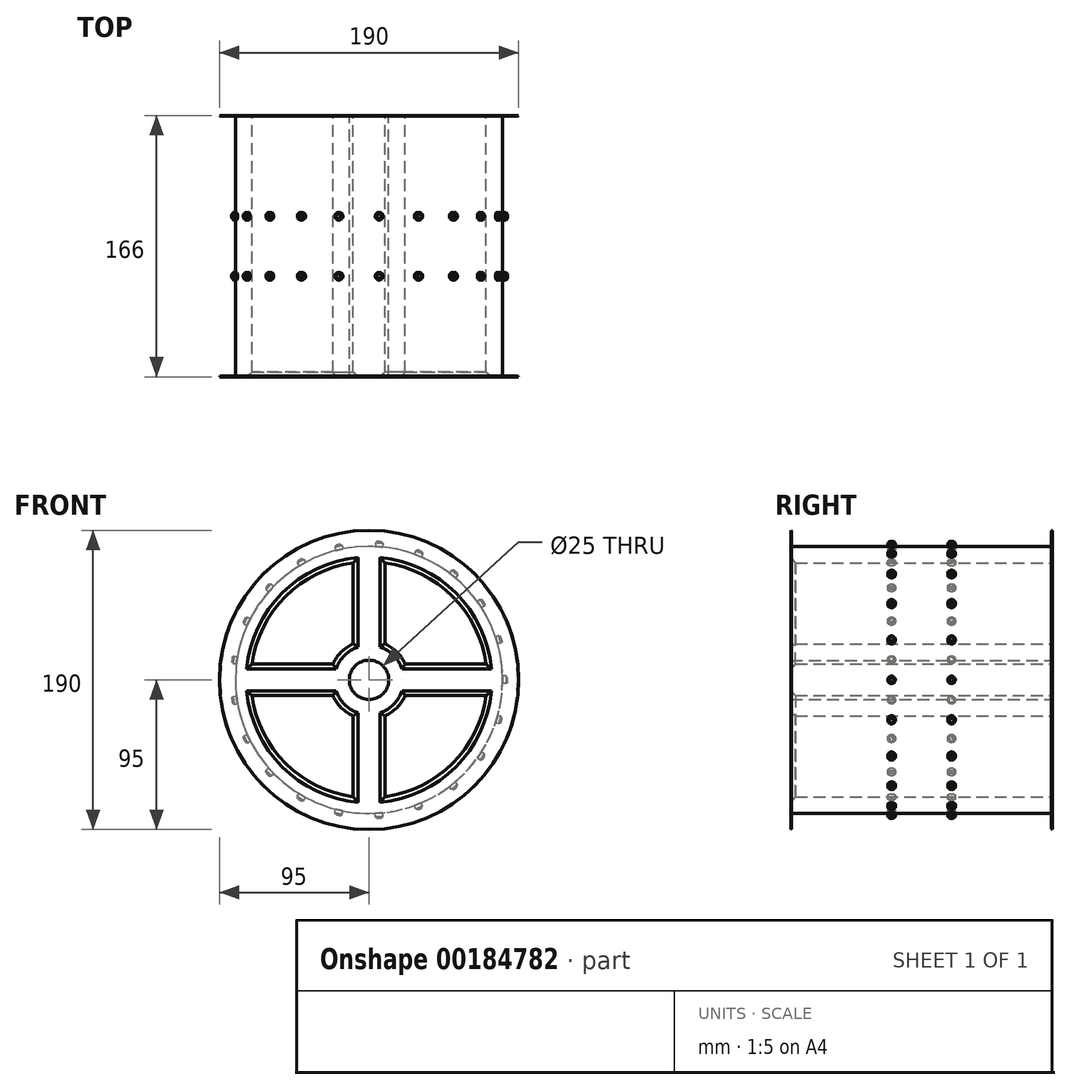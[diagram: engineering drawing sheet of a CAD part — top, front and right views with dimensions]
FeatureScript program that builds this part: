
annotation { "Feature Type Name" : "Feature", "Feature Type Description" : "" }
export const myFeature = defineFeature(function(context is Context, id is Id, definition is map)
    precondition{}
    {
        {
            var Q0;
            Q0=qCreatedBy(makeId("Front.planeOp"),FACE);
            var sketch = newSketch(context, id + "F0", { "sketchPlane" : qUnion([Q0])});
            skCircle(sketch, "E0", {"center": v(0, 0) * mm, "radius": 84.9 * mm});
            skSolve(sketch);
        }
        {
            var Q0;
            Q0=makeQuery(id+"F0.imprint","IMPRINT",FACE,{"disambiguationData":[TD([[makeQuery(id+"F0.imprint","IMPRINT",EDGE,{"derivedFrom":sQuery(id+"F0.wireOp",EDGE,"E0")}),1.0]])]});
            extrude(context, id + "F1", {"entities" : qUnion([Q0]), "depth" : 166 * mm});
        }
        {
            var Q0;
            Q0=makeQuery(id+"F1.opExtrude","CAP_FACE",FACE,{"disambiguationData":[OSD([sQuery(id+"F0.wireOp",EDGE,"E0")])],"isStart":true});
            var sketch = newSketch(context, id + "F2", { "sketchPlane" : qUnion([Q0])});
            skCircle(sketch, "E1", {"center": v(0, 0) * mm, "radius": 95 * mm});
            skSolve(sketch);
        }
        {
            var Q0;
            Q0=makeQuery(id+"F2.imprint","IMPRINT",FACE,{"disambiguationData":[TD([[makeQuery(id+"F2.imprint","IMPRINT",EDGE,{"derivedFrom":sQuery(id+"F2.wireOp",EDGE,"E1")}),1.0]])]});
            var Q1;
            Q1=sQuery(id+"F2.wireOp",EDGE,"E1");
            extrude(context, id + "F3", {"entities" : qUnion([Q0]), "operationType" : NewBodyOperationType.ADD, "surfaceEntities" : qUnion([Q1]), "oppositeDirection" : true, "depth" : .5 * mm});
        }
        {
            var Q0;
            Q0=makeQuery(id+"F1.opExtrude","CAP_FACE",FACE,{"disambiguationData":[OSD([sQuery(id+"F0.wireOp",EDGE,"E0")])],"isStart":false});
            var sketch = newSketch(context, id + "F4", { "sketchPlane" : qUnion([Q0])});
            skCircle(sketch, "E2", {"center": v(0, 0) * mm, "radius": 95 * mm});
            skSolve(sketch);
        }
        {
            var Q0;
            Q0=makeQuery(id+"F4.imprint","IMPRINT",FACE,{"disambiguationData":[TD([[makeQuery(id+"F4.imprint","IMPRINT",EDGE,{"derivedFrom":sQuery(id+"F4.wireOp",EDGE,"E2")}),1.0]])]});
            var Q1;
            Q1=sQuery(id+"F4.wireOp",EDGE,"E2");
            extrude(context, id + "F5", {"entities" : qUnion([Q0]), "operationType" : NewBodyOperationType.ADD, "surfaceEntities" : qUnion([Q1]), "oppositeDirection" : true, "depth" : .5 * mm});
        }
        {
            var Q0;
            Q0=qCreatedBy(makeId("Right.planeOp"),FACE);
            var sketch = newSketch(context, id + "F6", { "sketchPlane" : qUnion([Q0])});
            skCircle(sketch, "E3", {"center": v(-63.95, 0) * mm, "radius": 2.39 * mm});
            skLineSegment(sketch, "E4", {"start": v(-83, -58.64) * mm, "end": v(-83, 58.38) * mm});
            skCircle(sketch, "E5.MirrorC", {"center": v(-102.05, 0) * mm, "radius": 2.39 * mm});
            skSolve(sketch);
        }
        {
            var Q0;
            Q0 = qSketchRegion(id + "F6", true);
            extrude(context, id + "F7", {"entities" : qUnion([Q0]), "depth" : 88 * mm});
        }
        {
            var Q0;
            Q0=makeQuery(id+"F7.opExtrude","CAP_EDGE",EDGE,{"disambiguationData":[OSD([sQuery(id+"F6.wireOp",EDGE,"E3")])],"isStart":false});
            chamfer(context, id + "F8", {"entities" : qUnion([Q0]), "width" : 1 * mm, "tangentPropagation" : true});
        }
        {
            var Q0;
            Q0=makeQuery(id+"F7.opExtrude","SWEPT_BODY",BODY,{"disambiguationData":[OSD([sQuery(id+"F6.wireOp",EDGE,"E3")])]});
            var Q1;
            Q1=makeQuery(id+"F1.opExtrude","SWEPT_FACE",FACE,{"disambiguationData":[OSD([sQuery(id+"F0.wireOp",EDGE,"E0")])]});
            var Q2;
            Q2=makeQuery(id+"F1.opExtrude","SWEPT_BODY",BODY,{"disambiguationData":[OSD([sQuery(id+"F0.wireOp",EDGE,"E0")])]});
            circularPattern(context, id + "F9", {"operationType" : NewBodyOperationType.ADD, "entities" : qUnion([Q0]), "axis" : qUnion([Q1]), "angle" : 17.14 * degree, "instanceCount" : 21});
        }
        {
            var Q0;
            Q0=makeQuery(id+"F7.opExtrude","CAP_EDGE",EDGE,{"disambiguationData":[OSD([sQuery(id+"F6.wireOp",EDGE,"E5.MirrorC")])],"isStart":false});
            chamfer(context, id + "F10", {"entities" : qUnion([Q0]), "width" : 1 * mm, "tangentPropagation" : true});
        }
        {
            var Q0;
            Q0=makeQuery(id+"F7.opExtrude","SWEPT_BODY",BODY,{"disambiguationData":[OSD([sQuery(id+"F6.wireOp",EDGE,"E5.MirrorC")])]});
            var Q1;
            Q1=makeQuery(id+"F1.opExtrude","SWEPT_FACE",FACE,{"disambiguationData":[OSD([sQuery(id+"F0.wireOp",EDGE,"E0")])]});
            circularPattern(context, id + "F11", {"operationType" : NewBodyOperationType.ADD, "entities" : qUnion([Q0]), "axis" : qUnion([Q1]), "angle" : 17.14 * degree, "instanceCount" : 22});
        }
        {
            var Q0;
            Q0=makeQuery(id+"F3.opExtrude","CAP_EDGE",EDGE,{"disambiguationData":[OSD([sQuery(id+"F2.wireOp",EDGE,"E1")])],"isStart":false});
            var Q1;
            Q1=makeQuery(id+"F5.opExtrude","CAP_EDGE",EDGE,{"disambiguationData":[OSD([sQuery(id+"F4.wireOp",EDGE,"E2")])],"isStart":false});
            chamfer(context, id + "F12", {"entities" : qUnion([Q0, Q1]), "width" : .5 * mm, "tangentPropagation" : true});
        }
        {
            var Q0;
            {var subQ0=sQuery(id+"F0.wireOp",EDGE,"E0");Q0=makeQuery(id+"F3.boolean.opBoolean","MERGE",FACE,{"derivedFrom":[makeQuery(id+"F1.opExtrude","CAP_FACE",FACE,{"disambiguationData":[OSD([subQ0])],"isStart":true}),makeQuery(id+"F3.opExtrude","CAP_FACE",FACE,{"disambiguationData":[OSD([subQ0,sQuery(id+"F2.wireOp",EDGE,"E1")])],"isStart":true})]});}
            var sketch = newSketch(context, id + "F13", { "sketchPlane" : qUnion([Q0])});
            skCircle(sketch, "E6", {"center": v(0, 0) * mm, "radius": 75 * mm});
            skCircle(sketch, "E7", {"center": v(0, 0) * mm, "radius": 25 * mm});
            skCircle(sketch, "E8", {"center": v(0, 0) * mm, "radius": 12.5 * mm});
            skLineSegment(sketch, "E9", {"start": v(25, 0) * mm, "end": v(75, 0) * mm});
            skLineSegment(sketch, "E10", {"start": v(-25, 0) * mm, "end": v(-75, 0) * mm});
            skLineSegment(sketch, "E11", {"start": v(0, -25) * mm, "end": v(0, -75) * mm});
            skLineSegment(sketch, "E12", {"start": v(0, 25) * mm, "end": v(0, 75) * mm});
            skLineSegment(sketch, "E13", {"start": v(-22.91, 10) * mm, "end": v(-74.33, 10) * mm});
            skLineSegment(sketch, "E14", {"start": v(-22.91, -10) * mm, "end": v(-74.33, -10) * mm});
            skLineSegment(sketch, "E15", {"start": v(-10, -22.91) * mm, "end": v(-10, -74.33) * mm});
            skLineSegment(sketch, "E16", {"start": v(10, -22.91) * mm, "end": v(10, -74.33) * mm});
            skLineSegment(sketch, "E17", {"start": v(22.91, -10) * mm, "end": v(74.33, -10) * mm});
            skLineSegment(sketch, "E18", {"start": v(22.91, 10) * mm, "end": v(74.33, 10) * mm});
            skLineSegment(sketch, "E19", {"start": v(10, 22.91) * mm, "end": v(10, 74.33) * mm});
            skLineSegment(sketch, "E20", {"start": v(-10, 22.91) * mm, "end": v(-10, 74.33) * mm});
            skSolve(sketch);
        }
        {
            var Q0;
            {var subQ0=sQuery(id+"F13.wireOp",EDGE,"E13");Q0=makeQuery(id+"F13.imprint","IMPRINT",FACE,{"disambiguationData":[TD([[makeQuery(id+"F13.imprint","IMPRINT",EDGE,{"derivedFrom":subQ0}),-1.0]])]});}
            var Q1;
            {var subQ0=sQuery(id+"F13.wireOp",EDGE,"E18");Q1=makeQuery(id+"F13.imprint","IMPRINT",FACE,{"disambiguationData":[TD([[makeQuery(id+"F13.imprint","IMPRINT",EDGE,{"derivedFrom":subQ0}),1.0]])]});}
            var Q2;
            {var subQ0=sQuery(id+"F13.wireOp",EDGE,"E14");Q2=makeQuery(id+"F13.imprint","IMPRINT",FACE,{"disambiguationData":[TD([[makeQuery(id+"F13.imprint","IMPRINT",EDGE,{"derivedFrom":subQ0}),1.0]])]});}
            var Q3;
            {var subQ0=sQuery(id+"F13.wireOp",EDGE,"E16");Q3=makeQuery(id+"F13.imprint","IMPRINT",FACE,{"disambiguationData":[TD([[makeQuery(id+"F13.imprint","IMPRINT",EDGE,{"derivedFrom":subQ0}),1.0]])]});}
            var Q4;
            Q4=makeQuery(id+"F13.imprint","IMPRINT",FACE,{"disambiguationData":[TD([[makeQuery(id+"F13.imprint","IMPRINT",EDGE,{"derivedFrom":sQuery(id+"F13.wireOp",EDGE,"E8")}),1.0]])]});
            extrude(context, id + "F14", {"entities" : qUnion([Q0, Q1, Q2, Q3, Q4]), "operationType" : NewBodyOperationType.REMOVE, "endBound" : BoundingType.THROUGH_ALL, "oppositeDirection" : true, "depth" : 25.4 * mm});
        }
        {
            var Q0;
            {var subQ0=sQuery(id+"F13.wireOp",EDGE,"E6");var subQ1=sQuery(id+"F0.wireOp",EDGE,"E0");Q0=makeQuery(id+"F14.boolean.opBoolean","INTERSECT",EDGE,{"derivedFrom":[makeQuery(id+"F5.boolean.opBoolean","MERGE",FACE,{"derivedFrom":[makeQuery(id+"F1.opExtrude","CAP_FACE",FACE,{"disambiguationData":[OSD([subQ1])],"isStart":false}),makeQuery(id+"F5.opExtrude","CAP_FACE",FACE,{"disambiguationData":[OSD([subQ1,sQuery(id+"F4.wireOp",EDGE,"E2")])],"isStart":true})]}),makeQuery(id+"F14.opExtrude","SWEPT_FACE",FACE,{"disambiguationData":[OSD([subQ0]),TDD([makeQuery(id+"F13.imprint","IMPRINT",EDGE,{"disambiguationData":[TD([[makeQuery(id+"F13.imprint","INTERSECT",VERTEX,{"derivedFrom":[subQ0,sQuery(id+"F13.wireOp",EDGE,"E18")]}),-1.0]])],"derivedFrom":subQ0})])]})]});}
            var Q1;
            {var subQ0=sQuery(id+"F0.wireOp",EDGE,"E0");Q1=makeQuery(id+"F14.boolean.opBoolean","INTERSECT",EDGE,{"derivedFrom":[makeQuery(id+"F5.boolean.opBoolean","MERGE",FACE,{"derivedFrom":[makeQuery(id+"F1.opExtrude","CAP_FACE",FACE,{"disambiguationData":[OSD([subQ0])],"isStart":false}),makeQuery(id+"F5.opExtrude","CAP_FACE",FACE,{"disambiguationData":[OSD([subQ0,sQuery(id+"F4.wireOp",EDGE,"E2")])],"isStart":true})]}),makeQuery(id+"F14.opExtrude","SWEPT_FACE",FACE,{"disambiguationData":[OSD([sQuery(id+"F13.wireOp",EDGE,"E19")])]})]});}
            var Q2;
            {var subQ0=sQuery(id+"F0.wireOp",EDGE,"E0");Q2=makeQuery(id+"F14.boolean.opBoolean","INTERSECT",EDGE,{"derivedFrom":[makeQuery(id+"F5.boolean.opBoolean","MERGE",FACE,{"derivedFrom":[makeQuery(id+"F1.opExtrude","CAP_FACE",FACE,{"disambiguationData":[OSD([subQ0])],"isStart":false}),makeQuery(id+"F5.opExtrude","CAP_FACE",FACE,{"disambiguationData":[OSD([subQ0,sQuery(id+"F4.wireOp",EDGE,"E2")])],"isStart":true})]}),makeQuery(id+"F14.opExtrude","SWEPT_FACE",FACE,{"disambiguationData":[OSD([sQuery(id+"F13.wireOp",EDGE,"E18")])]})]});}
            var Q3;
            {var subQ0=sQuery(id+"F13.wireOp",EDGE,"E7");var subQ1=sQuery(id+"F0.wireOp",EDGE,"E0");Q3=makeQuery(id+"F14.boolean.opBoolean","INTERSECT",EDGE,{"derivedFrom":[makeQuery(id+"F5.boolean.opBoolean","MERGE",FACE,{"derivedFrom":[makeQuery(id+"F1.opExtrude","CAP_FACE",FACE,{"disambiguationData":[OSD([subQ1])],"isStart":false}),makeQuery(id+"F5.opExtrude","CAP_FACE",FACE,{"disambiguationData":[OSD([subQ1,sQuery(id+"F4.wireOp",EDGE,"E2")])],"isStart":true})]}),makeQuery(id+"F14.opExtrude","SWEPT_FACE",FACE,{"disambiguationData":[OSD([subQ0]),TDD([makeQuery(id+"F13.imprint","IMPRINT",EDGE,{"disambiguationData":[TD([[makeQuery(id+"F13.imprint","INTERSECT",VERTEX,{"derivedFrom":[subQ0,sQuery(id+"F13.wireOp",EDGE,"E18")]}),-1.0]])],"derivedFrom":subQ0})])]})]});}
            var Q4;
            {var subQ0=sQuery(id+"F13.wireOp",EDGE,"E6");var subQ1=sQuery(id+"F0.wireOp",EDGE,"E0");Q4=makeQuery(id+"F14.boolean.opBoolean","INTERSECT",EDGE,{"derivedFrom":[makeQuery(id+"F5.boolean.opBoolean","MERGE",FACE,{"derivedFrom":[makeQuery(id+"F1.opExtrude","CAP_FACE",FACE,{"disambiguationData":[OSD([subQ1])],"isStart":false}),makeQuery(id+"F5.opExtrude","CAP_FACE",FACE,{"disambiguationData":[OSD([subQ1,sQuery(id+"F4.wireOp",EDGE,"E2")])],"isStart":true})]}),makeQuery(id+"F14.opExtrude","SWEPT_FACE",FACE,{"disambiguationData":[OSD([subQ0]),TDD([makeQuery(id+"F13.imprint","IMPRINT",EDGE,{"disambiguationData":[TD([[makeQuery(id+"F13.imprint","INTERSECT",VERTEX,{"derivedFrom":[subQ0,sQuery(id+"F13.wireOp",EDGE,"E13")]}),1.0]])],"derivedFrom":subQ0})])]})]});}
            var Q5;
            {var subQ0=sQuery(id+"F0.wireOp",EDGE,"E0");Q5=makeQuery(id+"F14.boolean.opBoolean","INTERSECT",EDGE,{"derivedFrom":[makeQuery(id+"F5.boolean.opBoolean","MERGE",FACE,{"derivedFrom":[makeQuery(id+"F1.opExtrude","CAP_FACE",FACE,{"disambiguationData":[OSD([subQ0])],"isStart":false}),makeQuery(id+"F5.opExtrude","CAP_FACE",FACE,{"disambiguationData":[OSD([subQ0,sQuery(id+"F4.wireOp",EDGE,"E2")])],"isStart":true})]}),makeQuery(id+"F14.opExtrude","SWEPT_FACE",FACE,{"disambiguationData":[OSD([sQuery(id+"F13.wireOp",EDGE,"E13")])]})]});}
            var Q6;
            {var subQ0=sQuery(id+"F13.wireOp",EDGE,"E7");var subQ1=sQuery(id+"F0.wireOp",EDGE,"E0");Q6=makeQuery(id+"F14.boolean.opBoolean","INTERSECT",EDGE,{"derivedFrom":[makeQuery(id+"F5.boolean.opBoolean","MERGE",FACE,{"derivedFrom":[makeQuery(id+"F1.opExtrude","CAP_FACE",FACE,{"disambiguationData":[OSD([subQ1])],"isStart":false}),makeQuery(id+"F5.opExtrude","CAP_FACE",FACE,{"disambiguationData":[OSD([subQ1,sQuery(id+"F4.wireOp",EDGE,"E2")])],"isStart":true})]}),makeQuery(id+"F14.opExtrude","SWEPT_FACE",FACE,{"disambiguationData":[OSD([subQ0]),TDD([makeQuery(id+"F13.imprint","IMPRINT",EDGE,{"disambiguationData":[TD([[makeQuery(id+"F13.imprint","INTERSECT",VERTEX,{"derivedFrom":[subQ0,sQuery(id+"F13.wireOp",EDGE,"E13")]}),1.0]])],"derivedFrom":subQ0})])]})]});}
            var Q7;
            {var subQ0=sQuery(id+"F0.wireOp",EDGE,"E0");Q7=makeQuery(id+"F14.boolean.opBoolean","INTERSECT",EDGE,{"derivedFrom":[makeQuery(id+"F5.boolean.opBoolean","MERGE",FACE,{"derivedFrom":[makeQuery(id+"F1.opExtrude","CAP_FACE",FACE,{"disambiguationData":[OSD([subQ0])],"isStart":false}),makeQuery(id+"F5.opExtrude","CAP_FACE",FACE,{"disambiguationData":[OSD([subQ0,sQuery(id+"F4.wireOp",EDGE,"E2")])],"isStart":true})]}),makeQuery(id+"F14.opExtrude","SWEPT_FACE",FACE,{"disambiguationData":[OSD([sQuery(id+"F13.wireOp",EDGE,"E20")])]})]});}
            var Q8;
            {var subQ0=sQuery(id+"F0.wireOp",EDGE,"E0");Q8=makeQuery(id+"F14.boolean.opBoolean","INTERSECT",EDGE,{"derivedFrom":[makeQuery(id+"F5.boolean.opBoolean","MERGE",FACE,{"derivedFrom":[makeQuery(id+"F1.opExtrude","CAP_FACE",FACE,{"disambiguationData":[OSD([subQ0])],"isStart":false}),makeQuery(id+"F5.opExtrude","CAP_FACE",FACE,{"disambiguationData":[OSD([subQ0,sQuery(id+"F4.wireOp",EDGE,"E2")])],"isStart":true})]}),makeQuery(id+"F14.opExtrude","SWEPT_FACE",FACE,{"disambiguationData":[OSD([sQuery(id+"F13.wireOp",EDGE,"E14")])]})]});}
            var Q9;
            {var subQ0=sQuery(id+"F13.wireOp",EDGE,"E6");var subQ1=sQuery(id+"F0.wireOp",EDGE,"E0");Q9=makeQuery(id+"F14.boolean.opBoolean","INTERSECT",EDGE,{"derivedFrom":[makeQuery(id+"F5.boolean.opBoolean","MERGE",FACE,{"derivedFrom":[makeQuery(id+"F1.opExtrude","CAP_FACE",FACE,{"disambiguationData":[OSD([subQ1])],"isStart":false}),makeQuery(id+"F5.opExtrude","CAP_FACE",FACE,{"disambiguationData":[OSD([subQ1,sQuery(id+"F4.wireOp",EDGE,"E2")])],"isStart":true})]}),makeQuery(id+"F14.opExtrude","SWEPT_FACE",FACE,{"disambiguationData":[OSD([subQ0]),TDD([makeQuery(id+"F13.imprint","IMPRINT",EDGE,{"disambiguationData":[TD([[makeQuery(id+"F13.imprint","INTERSECT",VERTEX,{"derivedFrom":[subQ0,sQuery(id+"F13.wireOp",EDGE,"E14")]}),-1.0]])],"derivedFrom":subQ0})])]})]});}
            var Q10;
            {var subQ0=sQuery(id+"F13.wireOp",EDGE,"E7");var subQ1=sQuery(id+"F0.wireOp",EDGE,"E0");Q10=makeQuery(id+"F14.boolean.opBoolean","INTERSECT",EDGE,{"derivedFrom":[makeQuery(id+"F5.boolean.opBoolean","MERGE",FACE,{"derivedFrom":[makeQuery(id+"F1.opExtrude","CAP_FACE",FACE,{"disambiguationData":[OSD([subQ1])],"isStart":false}),makeQuery(id+"F5.opExtrude","CAP_FACE",FACE,{"disambiguationData":[OSD([subQ1,sQuery(id+"F4.wireOp",EDGE,"E2")])],"isStart":true})]}),makeQuery(id+"F14.opExtrude","SWEPT_FACE",FACE,{"disambiguationData":[OSD([subQ0]),TDD([makeQuery(id+"F13.imprint","IMPRINT",EDGE,{"disambiguationData":[TD([[makeQuery(id+"F13.imprint","INTERSECT",VERTEX,{"derivedFrom":[subQ0,sQuery(id+"F13.wireOp",EDGE,"E14")]}),-1.0]])],"derivedFrom":subQ0})])]})]});}
            var Q11;
            {var subQ0=sQuery(id+"F0.wireOp",EDGE,"E0");Q11=makeQuery(id+"F14.boolean.opBoolean","INTERSECT",EDGE,{"derivedFrom":[makeQuery(id+"F5.boolean.opBoolean","MERGE",FACE,{"derivedFrom":[makeQuery(id+"F1.opExtrude","CAP_FACE",FACE,{"disambiguationData":[OSD([subQ0])],"isStart":false}),makeQuery(id+"F5.opExtrude","CAP_FACE",FACE,{"disambiguationData":[OSD([subQ0,sQuery(id+"F4.wireOp",EDGE,"E2")])],"isStart":true})]}),makeQuery(id+"F14.opExtrude","SWEPT_FACE",FACE,{"disambiguationData":[OSD([sQuery(id+"F13.wireOp",EDGE,"E15")])]})]});}
            var Q12;
            {var subQ0=sQuery(id+"F0.wireOp",EDGE,"E0");Q12=makeQuery(id+"F14.boolean.opBoolean","INTERSECT",EDGE,{"derivedFrom":[makeQuery(id+"F5.boolean.opBoolean","MERGE",FACE,{"derivedFrom":[makeQuery(id+"F1.opExtrude","CAP_FACE",FACE,{"disambiguationData":[OSD([subQ0])],"isStart":false}),makeQuery(id+"F5.opExtrude","CAP_FACE",FACE,{"disambiguationData":[OSD([subQ0,sQuery(id+"F4.wireOp",EDGE,"E2")])],"isStart":true})]}),makeQuery(id+"F14.opExtrude","SWEPT_FACE",FACE,{"disambiguationData":[OSD([sQuery(id+"F13.wireOp",EDGE,"E16")])]})]});}
            var Q13;
            {var subQ0=sQuery(id+"F13.wireOp",EDGE,"E7");var subQ1=sQuery(id+"F0.wireOp",EDGE,"E0");Q13=makeQuery(id+"F14.boolean.opBoolean","INTERSECT",EDGE,{"derivedFrom":[makeQuery(id+"F5.boolean.opBoolean","MERGE",FACE,{"derivedFrom":[makeQuery(id+"F1.opExtrude","CAP_FACE",FACE,{"disambiguationData":[OSD([subQ1])],"isStart":false}),makeQuery(id+"F5.opExtrude","CAP_FACE",FACE,{"disambiguationData":[OSD([subQ1,sQuery(id+"F4.wireOp",EDGE,"E2")])],"isStart":true})]}),makeQuery(id+"F14.opExtrude","SWEPT_FACE",FACE,{"disambiguationData":[OSD([subQ0]),TDD([makeQuery(id+"F13.imprint","IMPRINT",EDGE,{"disambiguationData":[TD([[makeQuery(id+"F13.imprint","INTERSECT",VERTEX,{"derivedFrom":[subQ0,sQuery(id+"F13.wireOp",EDGE,"E16")]}),-1.0]])],"derivedFrom":subQ0})])]})]});}
            var Q14;
            {var subQ0=sQuery(id+"F0.wireOp",EDGE,"E0");Q14=makeQuery(id+"F14.boolean.opBoolean","INTERSECT",EDGE,{"derivedFrom":[makeQuery(id+"F5.boolean.opBoolean","MERGE",FACE,{"derivedFrom":[makeQuery(id+"F1.opExtrude","CAP_FACE",FACE,{"disambiguationData":[OSD([subQ0])],"isStart":false}),makeQuery(id+"F5.opExtrude","CAP_FACE",FACE,{"disambiguationData":[OSD([subQ0,sQuery(id+"F4.wireOp",EDGE,"E2")])],"isStart":true})]}),makeQuery(id+"F14.opExtrude","SWEPT_FACE",FACE,{"disambiguationData":[OSD([sQuery(id+"F13.wireOp",EDGE,"E17")])]})]});}
            var Q15;
            {var subQ0=sQuery(id+"F13.wireOp",EDGE,"E6");var subQ1=sQuery(id+"F0.wireOp",EDGE,"E0");Q15=makeQuery(id+"F14.boolean.opBoolean","INTERSECT",EDGE,{"derivedFrom":[makeQuery(id+"F5.boolean.opBoolean","MERGE",FACE,{"derivedFrom":[makeQuery(id+"F1.opExtrude","CAP_FACE",FACE,{"disambiguationData":[OSD([subQ1])],"isStart":false}),makeQuery(id+"F5.opExtrude","CAP_FACE",FACE,{"disambiguationData":[OSD([subQ1,sQuery(id+"F4.wireOp",EDGE,"E2")])],"isStart":true})]}),makeQuery(id+"F14.opExtrude","SWEPT_FACE",FACE,{"disambiguationData":[OSD([subQ0]),TDD([makeQuery(id+"F13.imprint","IMPRINT",EDGE,{"disambiguationData":[TD([[makeQuery(id+"F13.imprint","INTERSECT",VERTEX,{"derivedFrom":[subQ0,sQuery(id+"F13.wireOp",EDGE,"E16")]}),-1.0]])],"derivedFrom":subQ0})])]})]});}
            var Q16;
            {var subQ0=sQuery(id+"F13.wireOp",EDGE,"E6");Q16=makeQuery(id+"F14.boolean.opBoolean","COPY",EDGE,{"derivedFrom":makeQuery(id+"F14.opExtrude","CAP_EDGE",EDGE,{"disambiguationData":[OSD([subQ0]),TDD([makeQuery(id+"F13.imprint","IMPRINT",EDGE,{"disambiguationData":[TD([[makeQuery(id+"F13.imprint","INTERSECT",VERTEX,{"derivedFrom":[subQ0,sQuery(id+"F13.wireOp",EDGE,"E18")]}),-1.0]])],"derivedFrom":subQ0})])],"isStart":true})});}
            var Q17;
            Q17=makeQuery(id+"F14.boolean.opBoolean","COPY",EDGE,{"derivedFrom":makeQuery(id+"F14.opExtrude","CAP_EDGE",EDGE,{"disambiguationData":[OSD([sQuery(id+"F13.wireOp",EDGE,"E19")])],"isStart":true})});
            var Q18;
            {var subQ0=sQuery(id+"F13.wireOp",EDGE,"E7");Q18=makeQuery(id+"F14.boolean.opBoolean","COPY",EDGE,{"derivedFrom":makeQuery(id+"F14.opExtrude","CAP_EDGE",EDGE,{"disambiguationData":[OSD([subQ0]),TDD([makeQuery(id+"F13.imprint","IMPRINT",EDGE,{"disambiguationData":[TD([[makeQuery(id+"F13.imprint","INTERSECT",VERTEX,{"derivedFrom":[subQ0,sQuery(id+"F13.wireOp",EDGE,"E18")]}),-1.0]])],"derivedFrom":subQ0})])],"isStart":true})});}
            var Q19;
            Q19=makeQuery(id+"F14.boolean.opBoolean","COPY",EDGE,{"derivedFrom":makeQuery(id+"F14.opExtrude","CAP_EDGE",EDGE,{"disambiguationData":[OSD([sQuery(id+"F13.wireOp",EDGE,"E18")])],"isStart":true})});
            var Q20;
            {var subQ0=sQuery(id+"F13.wireOp",EDGE,"E6");Q20=makeQuery(id+"F14.boolean.opBoolean","COPY",EDGE,{"derivedFrom":makeQuery(id+"F14.opExtrude","CAP_EDGE",EDGE,{"disambiguationData":[OSD([subQ0]),TDD([makeQuery(id+"F13.imprint","IMPRINT",EDGE,{"disambiguationData":[TD([[makeQuery(id+"F13.imprint","INTERSECT",VERTEX,{"derivedFrom":[subQ0,sQuery(id+"F13.wireOp",EDGE,"E16")]}),-1.0]])],"derivedFrom":subQ0})])],"isStart":true})});}
            var Q21;
            Q21=makeQuery(id+"F14.boolean.opBoolean","COPY",EDGE,{"derivedFrom":makeQuery(id+"F14.opExtrude","CAP_EDGE",EDGE,{"disambiguationData":[OSD([sQuery(id+"F13.wireOp",EDGE,"E17")])],"isStart":true})});
            var Q22;
            {var subQ0=sQuery(id+"F13.wireOp",EDGE,"E7");Q22=makeQuery(id+"F14.boolean.opBoolean","COPY",EDGE,{"derivedFrom":makeQuery(id+"F14.opExtrude","CAP_EDGE",EDGE,{"disambiguationData":[OSD([subQ0]),TDD([makeQuery(id+"F13.imprint","IMPRINT",EDGE,{"disambiguationData":[TD([[makeQuery(id+"F13.imprint","INTERSECT",VERTEX,{"derivedFrom":[subQ0,sQuery(id+"F13.wireOp",EDGE,"E16")]}),-1.0]])],"derivedFrom":subQ0})])],"isStart":true})});}
            var Q23;
            Q23=makeQuery(id+"F14.boolean.opBoolean","COPY",EDGE,{"derivedFrom":makeQuery(id+"F14.opExtrude","CAP_EDGE",EDGE,{"disambiguationData":[OSD([sQuery(id+"F13.wireOp",EDGE,"E16")])],"isStart":true})});
            var Q24;
            Q24=makeQuery(id+"F14.boolean.opBoolean","COPY",EDGE,{"derivedFrom":makeQuery(id+"F14.opExtrude","CAP_EDGE",EDGE,{"disambiguationData":[OSD([sQuery(id+"F13.wireOp",EDGE,"E20")])],"isStart":true})});
            var Q25;
            {var subQ0=sQuery(id+"F13.wireOp",EDGE,"E6");Q25=makeQuery(id+"F14.boolean.opBoolean","COPY",EDGE,{"derivedFrom":makeQuery(id+"F14.opExtrude","CAP_EDGE",EDGE,{"disambiguationData":[OSD([subQ0]),TDD([makeQuery(id+"F13.imprint","IMPRINT",EDGE,{"disambiguationData":[TD([[makeQuery(id+"F13.imprint","INTERSECT",VERTEX,{"derivedFrom":[subQ0,sQuery(id+"F13.wireOp",EDGE,"E13")]}),1.0]])],"derivedFrom":subQ0})])],"isStart":true})});}
            var Q26;
            {var subQ0=sQuery(id+"F13.wireOp",EDGE,"E7");Q26=makeQuery(id+"F14.boolean.opBoolean","COPY",EDGE,{"derivedFrom":makeQuery(id+"F14.opExtrude","CAP_EDGE",EDGE,{"disambiguationData":[OSD([subQ0]),TDD([makeQuery(id+"F13.imprint","IMPRINT",EDGE,{"disambiguationData":[TD([[makeQuery(id+"F13.imprint","INTERSECT",VERTEX,{"derivedFrom":[subQ0,sQuery(id+"F13.wireOp",EDGE,"E13")]}),1.0]])],"derivedFrom":subQ0})])],"isStart":true})});}
            var Q27;
            Q27=makeQuery(id+"F14.boolean.opBoolean","COPY",EDGE,{"derivedFrom":makeQuery(id+"F14.opExtrude","CAP_EDGE",EDGE,{"disambiguationData":[OSD([sQuery(id+"F13.wireOp",EDGE,"E13")])],"isStart":true})});
            var Q28;
            {var subQ0=sQuery(id+"F13.wireOp",EDGE,"E7");Q28=makeQuery(id+"F14.boolean.opBoolean","COPY",EDGE,{"derivedFrom":makeQuery(id+"F14.opExtrude","CAP_EDGE",EDGE,{"disambiguationData":[OSD([subQ0]),TDD([makeQuery(id+"F13.imprint","IMPRINT",EDGE,{"disambiguationData":[TD([[makeQuery(id+"F13.imprint","INTERSECT",VERTEX,{"derivedFrom":[subQ0,sQuery(id+"F13.wireOp",EDGE,"E14")]}),-1.0]])],"derivedFrom":subQ0})])],"isStart":true})});}
            var Q29;
            Q29=makeQuery(id+"F14.boolean.opBoolean","COPY",EDGE,{"derivedFrom":makeQuery(id+"F14.opExtrude","CAP_EDGE",EDGE,{"disambiguationData":[OSD([sQuery(id+"F13.wireOp",EDGE,"E15")])],"isStart":true})});
            var Q30;
            Q30=makeQuery(id+"F14.boolean.opBoolean","COPY",EDGE,{"derivedFrom":makeQuery(id+"F14.opExtrude","CAP_EDGE",EDGE,{"disambiguationData":[OSD([sQuery(id+"F13.wireOp",EDGE,"E14")])],"isStart":true})});
            var Q31;
            {var subQ0=sQuery(id+"F13.wireOp",EDGE,"E6");Q31=makeQuery(id+"F14.boolean.opBoolean","COPY",EDGE,{"derivedFrom":makeQuery(id+"F14.opExtrude","CAP_EDGE",EDGE,{"disambiguationData":[OSD([subQ0]),TDD([makeQuery(id+"F13.imprint","IMPRINT",EDGE,{"disambiguationData":[TD([[makeQuery(id+"F13.imprint","INTERSECT",VERTEX,{"derivedFrom":[subQ0,sQuery(id+"F13.wireOp",EDGE,"E14")]}),-1.0]])],"derivedFrom":subQ0})])],"isStart":true})});}
            chamfer(context, id + "F15", {"entities" : qUnion([Q0, Q1, Q2, Q3, Q4, Q5, Q6, Q7, Q8, Q9, Q10, Q11, Q12, Q13, Q14, Q15, Q16, Q17, Q18, Q19, Q20, Q21, Q22, Q23, Q24, Q25, Q26, Q27, Q28, Q29, Q30, Q31]), "width" : 3 * mm});
        }
    });
